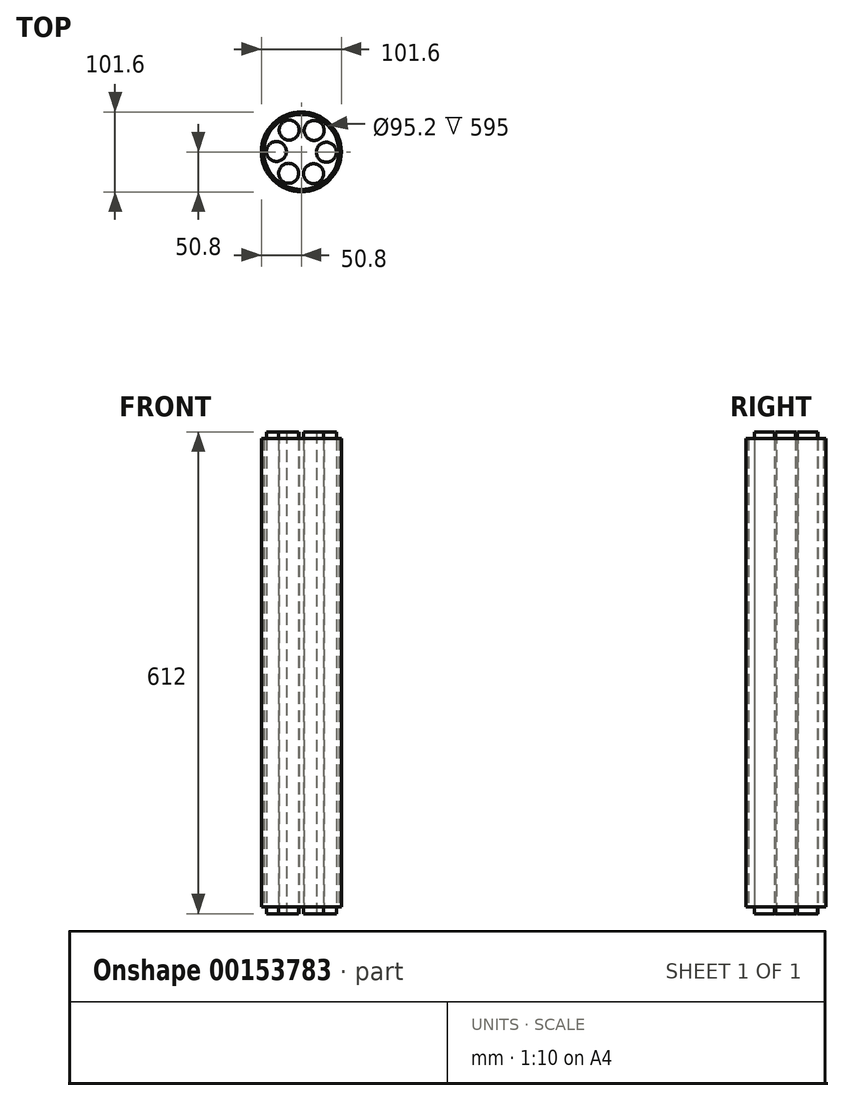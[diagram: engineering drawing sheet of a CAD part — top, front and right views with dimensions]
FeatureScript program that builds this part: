
annotation { "Feature Type Name" : "Feature", "Feature Type Description" : "" }
export const myFeature = defineFeature(function(context is Context, id is Id, definition is map)
    precondition{}
    {
        {
            var Q0;
            Q0=qCreatedBy(makeId("Top.planeOp"),FACE);
            var sketch = newSketch(context, id + "F0", { "sketchPlane" : qUnion([Q0])});
            skCircle(sketch, "E0", {"center": v(0, 0) * mm, "radius": 50.8 * mm});
            skCircle(sketch, "E1", {"center": v(0, 0) * mm, "radius": 47.6 * mm});
            skSolve(sketch);
        }
        {
            var Q0;
            Q0 = qSketchRegion(id + "F0", true);
            extrude(context, id + "F1", {"entities" : qUnion([Q0]), "depth" : 595 * mm});
        }
        {
            var Q0;
            Q0=qCreatedBy(makeId("Top.planeOp"),FACE);
            cPlane(context, id + "F2", {"entities" : qUnion([Q0]), "cplaneType" : CPlaneType.OFFSET, "offset" : 595 * mm / 2, "width" : 150 * mm, "height" : 150 * mm});
        }
        {
            var Q0;
            Q0=qCreatedBy(id+"F2.planeOp",FACE);
            var sketch = newSketch(context, id + "F3", { "sketchPlane" : qUnion([Q0])});
            skCircle(sketch, "E2.0", {"center": v(0, 0) * mm, "radius": 31.73 * mm, "construction": true});
            skCircle(sketch, "E3", {"center": v(-15.5, 27.68) * mm, "radius": 12.7 * mm});
            skCircle(sketch, "E4.1.1", {"center": v(-31.72, 0.42) * mm, "radius": 12.7 * mm});
            skCircle(sketch, "E4.2.1", {"center": v(-16.22, -27.26) * mm, "radius": 12.7 * mm});
            skCircle(sketch, "E4.3.1", {"center": v(15.5, -27.68) * mm, "radius": 12.7 * mm});
            skCircle(sketch, "E4.4.1", {"center": v(31.72, -0.42) * mm, "radius": 12.7 * mm});
            skCircle(sketch, "E4.5.1", {"center": v(16.22, 27.26) * mm, "radius": 12.7 * mm});
            skLineSegment(sketch, "E5", {"start": v(-1.8, 0.57) * mm, "end": v(-0.29, 2.09) * mm});
            skLineSegment(sketch, "E6", {"start": v(-15.5, 27.68) * mm, "end": v(-15.5, -9.22) * mm, "construction": true});
            skLineSegment(sketch, "E7.0", {"start": v(-0.5, 0.57) * mm, "end": v(-0.5, -11.83) * mm, "construction": true});
            skLineSegment(sketch, "E8", {"start": v(-0.5, -11.83) * mm, "end": v(-27.7, -11.83) * mm, "construction": true});
            skLineSegment(sketch, "E9", {"start": v(-27.7, -11.83) * mm, "end": v(-27.7, 12.97) * mm, "construction": true});
            skLineSegment(sketch, "E10", {"start": v(-27.7, 12.97) * mm, "end": v(-0.5, 12.97) * mm, "construction": true});
            skLineSegment(sketch, "E11", {"start": v(-0.5, 12.97) * mm, "end": v(-0.5, -11.83) * mm, "construction": true});
            skSolve(sketch);
        }
        {
            var Q0;
            Q0=makeQuery(id+"F3.imprint","IMPRINT",FACE,{"disambiguationData":[TD([[makeQuery(id+"F3.imprint","IMPRINT",EDGE,{"derivedFrom":sQuery(id+"F3.wireOp",EDGE,"E3")}),1.0]])]});
            var Q1;
            Q1=makeQuery(id+"F3.imprint","IMPRINT",FACE,{"disambiguationData":[TD([[makeQuery(id+"F3.imprint","IMPRINT",EDGE,{"derivedFrom":sQuery(id+"F3.wireOp",EDGE,"E4.5.1")}),1.0]])]});
            var Q2;
            Q2=makeQuery(id+"F3.imprint","IMPRINT",FACE,{"disambiguationData":[TD([[makeQuery(id+"F3.imprint","IMPRINT",EDGE,{"derivedFrom":sQuery(id+"F3.wireOp",EDGE,"E4.1.1")}),1.0]])]});
            var Q3;
            Q3=makeQuery(id+"F3.imprint","IMPRINT",FACE,{"disambiguationData":[TD([[makeQuery(id+"F3.imprint","IMPRINT",EDGE,{"derivedFrom":sQuery(id+"F3.wireOp",EDGE,"E4.4.1")}),1.0]])]});
            var Q4;
            Q4=makeQuery(id+"F3.imprint","IMPRINT",FACE,{"disambiguationData":[TD([[makeQuery(id+"F3.imprint","IMPRINT",EDGE,{"derivedFrom":sQuery(id+"F3.wireOp",EDGE,"E4.3.1")}),1.0]])]});
            var Q5;
            Q5=makeQuery(id+"F3.imprint","IMPRINT",FACE,{"disambiguationData":[TD([[makeQuery(id+"F3.imprint","IMPRINT",EDGE,{"derivedFrom":sQuery(id+"F3.wireOp",EDGE,"E4.2.1")}),1.0]])]});
            extrude(context, id + "F4", {"entities" : qUnion([Q0, Q1, Q2, Q3, Q4, Q5]), "endBound" : BoundingType.SYMMETRIC, "depth" : 604 * mm + 8 * mm});
        }
    });
